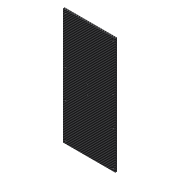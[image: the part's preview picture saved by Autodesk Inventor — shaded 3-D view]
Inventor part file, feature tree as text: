
AUTODESK INVENTOR PART (.ipt)
format: ipt  version: 2018 (Build 220112000, 112)  size: 163,840 bytes
history: native  units: mm
features: other x4, extrude x3, sketch x2, reference x2
ambient origin geometry x8: Origin, YZ Plane, XZ Plane, XY Plane, X Axis, Y Axis, Z Axis, Center Point
bodies: Volumenkörper1 (feature_tree)
feature tree (11):
  sketch  "Skizze1"  dims[d1=45.0mm d2=45.0mm]
  extrude  "Extrusion1"  Depth=45.0mm
  extrude  "Extrusion2"  Depth=10.0mm
  extrude  "Extrusion3"  Depth=3.0mm TaperAngle=0.0deg
  sketch  "Skizze2"  dims[d3=100.0mm d4=100.0mm d5=3.0mm d6=0.0mm d7=3.4mm d8=4.0mm d9=5.0mm d10=3.4mm d11=4.0mm d12=5.0mm d13=3.4mm d14=4.0mm d15=5.0mm d16=3.4mm d17=5.0mm d18=4.0mm d19=10.0mm d20=0.0mm d21=10.0mm d22=0.0mm d23=800.0mm d25=80.0mm d26=10.0mm d28=10.0mm d30=20.0mm d32=50.0mm d33=10.0mm d35=10.0mm]
  reference  "Referenz1"
  reference  "Referenz2"
  other  "<userpath>\OneDrive\Development\Mohne\03_Konstruktion\Mohne komplett.iam"
  other  "Mohne komplett.iam"
  other  "MPU 6050 IMU:1"
  other  "Base:1"
